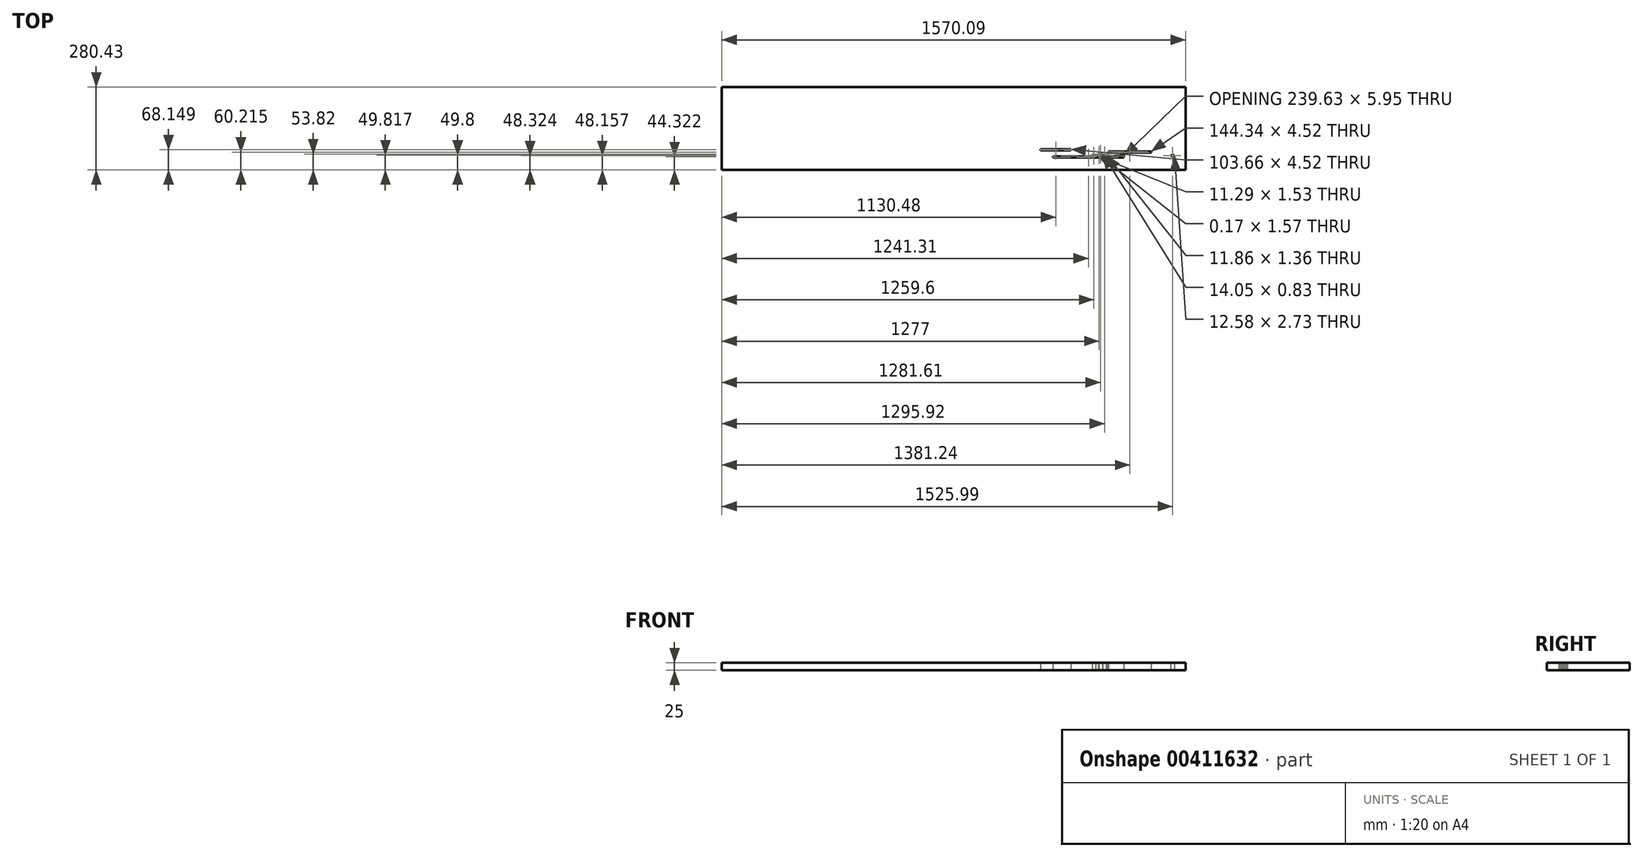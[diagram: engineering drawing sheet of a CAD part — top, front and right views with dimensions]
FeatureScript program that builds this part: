
annotation { "Feature Type Name" : "Feature", "Feature Type Description" : "" }
export const myFeature = defineFeature(function(context is Context, id is Id, definition is map)
    precondition{}
    {
        {
            var Q0;
            Q0=qCreatedBy(makeId("Top.planeOp"),FACE);
            var sketch = newSketch(context, id + "F0", { "sketchPlane" : qUnion([Q0])});
            skLineSegment(sketch, "E0.bottom", {"start": v(-5.5, 3.44) * mm, "end": v(233.85, 3.44) * mm});
            skLineSegment(sketch, "E0.top", {"start": v(-5.5, 7.96) * mm, "end": v(233.85, 7.96) * mm});
            skLineSegment(sketch, "E0.left", {"start": v(-5.5, 3.44) * mm, "end": v(-5.5, 7.96) * mm});
            skLineSegment(sketch, "E0.right", {"start": v(233.85, 3.44) * mm, "end": v(233.85, 7.96) * mm});
            skLineSegment(sketch, "E1.bottom", {"start": v(392.71, 9.05) * mm, "end": v(405.29, 9.05) * mm});
            skLineSegment(sketch, "E1.top", {"start": v(392.71, 11.78) * mm, "end": v(405.29, 11.78) * mm});
            skLineSegment(sketch, "E1.left", {"start": v(392.71, 9.05) * mm, "end": v(392.71, 11.78) * mm});
            skLineSegment(sketch, "E1.right", {"start": v(405.29, 9.05) * mm, "end": v(405.29, 11.78) * mm});
            skLineSegment(sketch, "E2.bottom", {"start": v(326.42, 20.04) * mm, "end": v(182.08, 20.04) * mm});
            skLineSegment(sketch, "E2.top", {"start": v(326.42, 24.57) * mm, "end": v(182.08, 24.57) * mm});
            skLineSegment(sketch, "E2.left", {"start": v(326.42, 20.04) * mm, "end": v(326.42, 24.57) * mm});
            skLineSegment(sketch, "E2.right", {"start": v(182.08, 20.04) * mm, "end": v(182.08, 24.57) * mm});
            skLineSegment(sketch, "E3.bottom", {"start": v(55.32, 27.98) * mm, "end": v(-48.34, 27.98) * mm});
            skLineSegment(sketch, "E3.top", {"start": v(55.32, 32.5) * mm, "end": v(-48.34, 32.5) * mm});
            skLineSegment(sketch, "E3.left", {"start": v(55.32, 27.98) * mm, "end": v(55.32, 32.5) * mm});
            skLineSegment(sketch, "E3.right", {"start": v(-48.34, 27.98) * mm, "end": v(-48.34, 32.5) * mm});
            skLineSegment(sketch, "E4.bottom", {"start": v(167.11, 3.44) * mm, "end": v(114.18, 3.44) * mm});
            skLineSegment(sketch, "E4.top", {"start": v(167.11, 7.96) * mm, "end": v(114.18, 7.96) * mm});
            skLineSegment(sketch, "E4.left", {"start": v(167.11, 3.44) * mm, "end": v(167.11, 7.96) * mm});
            skLineSegment(sketch, "E4.right", {"start": v(114.18, 3.44) * mm, "end": v(114.18, 7.96) * mm});
            skLineSegment(sketch, "E5.bottom", {"start": v(234.14, 4.63) * mm, "end": v(179.55, 4.63) * mm});
            skLineSegment(sketch, "E5.top", {"start": v(234.14, 9.39) * mm, "end": v(179.55, 9.39) * mm});
            skLineSegment(sketch, "E5.left", {"start": v(234.14, 4.63) * mm, "end": v(234.14, 9.39) * mm});
            skLineSegment(sketch, "E5.right", {"start": v(179.55, 4.63) * mm, "end": v(179.55, 9.39) * mm});
            skLineSegment(sketch, "E6.bottom", {"start": v(138.25, 9.48) * mm, "end": v(126.96, 9.48) * mm});
            skLineSegment(sketch, "E6.top", {"start": v(138.25, 11.01) * mm, "end": v(126.96, 11.01) * mm});
            skLineSegment(sketch, "E6.left", {"start": v(138.25, 9.48) * mm, "end": v(138.25, 11.01) * mm});
            skLineSegment(sketch, "E6.right", {"start": v(126.96, 9.48) * mm, "end": v(126.96, 11.01) * mm});
            skLineSegment(sketch, "E7.bottom", {"start": v(150.1, 11.1) * mm, "end": v(149.92, 11.1) * mm});
            skLineSegment(sketch, "E7.top", {"start": v(150.1, 12.67) * mm, "end": v(149.92, 12.67) * mm});
            skLineSegment(sketch, "E7.left", {"start": v(150.1, 11.1) * mm, "end": v(150.1, 12.67) * mm});
            skLineSegment(sketch, "E7.right", {"start": v(149.92, 11.1) * mm, "end": v(149.92, 12.67) * mm});
            skLineSegment(sketch, "E8.bottom", {"start": v(163, 12.59) * mm, "end": v(174.86, 12.59) * mm});
            skLineSegment(sketch, "E8.top", {"start": v(163, 11.23) * mm, "end": v(174.86, 11.23) * mm});
            skLineSegment(sketch, "E8.left", {"start": v(163, 12.59) * mm, "end": v(163, 11.23) * mm});
            skLineSegment(sketch, "E8.right", {"start": v(174.86, 12.59) * mm, "end": v(174.86, 11.23) * mm});
            skLineSegment(sketch, "E9.bottom", {"start": v(147.6, 15.5) * mm, "end": v(161.65, 15.5) * mm});
            skLineSegment(sketch, "E9.top", {"start": v(147.6, 16.32) * mm, "end": v(161.65, 16.32) * mm});
            skLineSegment(sketch, "E9.left", {"start": v(147.6, 15.5) * mm, "end": v(147.6, 16.32) * mm});
            skLineSegment(sketch, "E9.right", {"start": v(161.65, 15.5) * mm, "end": v(161.65, 16.32) * mm});
            skLineSegment(sketch, "E10.bottom", {"start": v(443.1, -37.91) * mm, "end": v(-1127, -37.91) * mm});
            skLineSegment(sketch, "E10.top", {"start": v(443.1, 242.52) * mm, "end": v(-1127, 242.52) * mm});
            skLineSegment(sketch, "E10.left", {"start": v(443.1, -37.91) * mm, "end": v(443.1, 242.52) * mm});
            skLineSegment(sketch, "E10.right", {"start": v(-1127, -37.91) * mm, "end": v(-1127, 242.52) * mm});
            skSolve(sketch);
        }
        {
            var Q0;
            Q0 = qSketchRegion(id + "F0", true);
            extrude(context, id + "F1", {"entities" : qUnion([Q0]), "depth" : 25 * mm});
        }
    });
